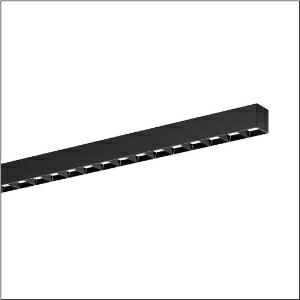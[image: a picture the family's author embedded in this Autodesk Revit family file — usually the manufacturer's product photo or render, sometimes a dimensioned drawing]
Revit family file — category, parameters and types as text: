
# Revit family: silica_r__21_51mx21tat4b_6284
name_source: partatom
category: Lighting Fixtures
units: mm (PartAtom-declared; Revit-internal decimal feet)

## family parameters
Cut with Voids When Loaded = No
Host = Face
Light Source = No
Part Type = Normal
Room Calculation Point = No
Round Connector Dimension = Use Diameter
Shared = No

## types (1)
- --- (1 x LED, 3720 lm, 32.2 W, 6500K)
    Apparent Load = 32 VA
    CIE Flux Codes = 85 99 100 100 100
    Color Rendering = 80
    Color Temperature = 6500K
    Default Elevation = 1800 mm
    Description = Silica® 21, office luminaire, primary light control with darklight reflector, of PMMA, black, CAT 2 (L<= 3000cd/m²), light emission: direct distribution, primary light characteristic: symmetric, installation type: surface-mounted, LED, rated luminous flux: 3.720lm, luminous efficacy: 110lm/W, light colour: 8tw, colour temperature: 2700..6500K, control gear: ECG DALI, with terminal, 3+2-pole, max. 2.5mm², mains connection: 220..240V, AC, 50/60Hz, rated input power: 33.8W, luminaire housing, of aluminium, jet black (RAL 9005), length: 1.204mm, width: 53mm, height: 53mm, protection rating (complete): IP20, insulation class (complete): insulation class I (protective earthing), certification: CE, permissible operating ambient temperature: 0..+35°C, standard: EN 50419, packaging unit: 1 piece
    Height = 0 mm  [stored 0 ft]
    Lamp = 1 x LED
    Lamp Light Flux = 3720 lm
    Lamp Power = 32.2 W
    Lamp count = 1
    Length = 1204 mm
    Luminous efficacy = 116 lm/W
    Manufacturer = Siteco
    ModVariant = No
    Model = 51MX21TAT4B
    Mounting Place = Ceiling
    Mounting Type = Recessed
    Number of Poles = 1
    OnlyDefault = Yes
    Power Factor = 1
    Product Name = Silica® 21
    Product group = office luminaire | ceiling recessed
    ProductGroupID = 400
    Protection Class = Protection class I
    Protection Degree = IP 20
    RLX_Detail_Level = 1
    RLX_Emergency_Light_Flux = 0 lm
    RLX_Emergency_Type = 0
    RLX_Emergency_Type_DB = No
    RlxData = <blob elided: 40261 chars, md5=1bbfb418>
    Socket = socket
    Standby Power = 0 W
    System Light Flux = 3720 lm
    System Power = 32 W
    Type Comments = individual setting
    Type Image = l_1335908.jpg
    URL = http://relux.com
    VarID = @adj_109873
    Voltage = 0 V
    Weight = 0.00 kg
    Width = 53 mm

note: [stored X ft] marks values corroborated as IEEE doubles in the binary element streams (Revit-internal decimal feet)

## geometry (parser evidence)
native form markers: Blend x4, Sweep x12
no freeform markers — native parametric forms only
